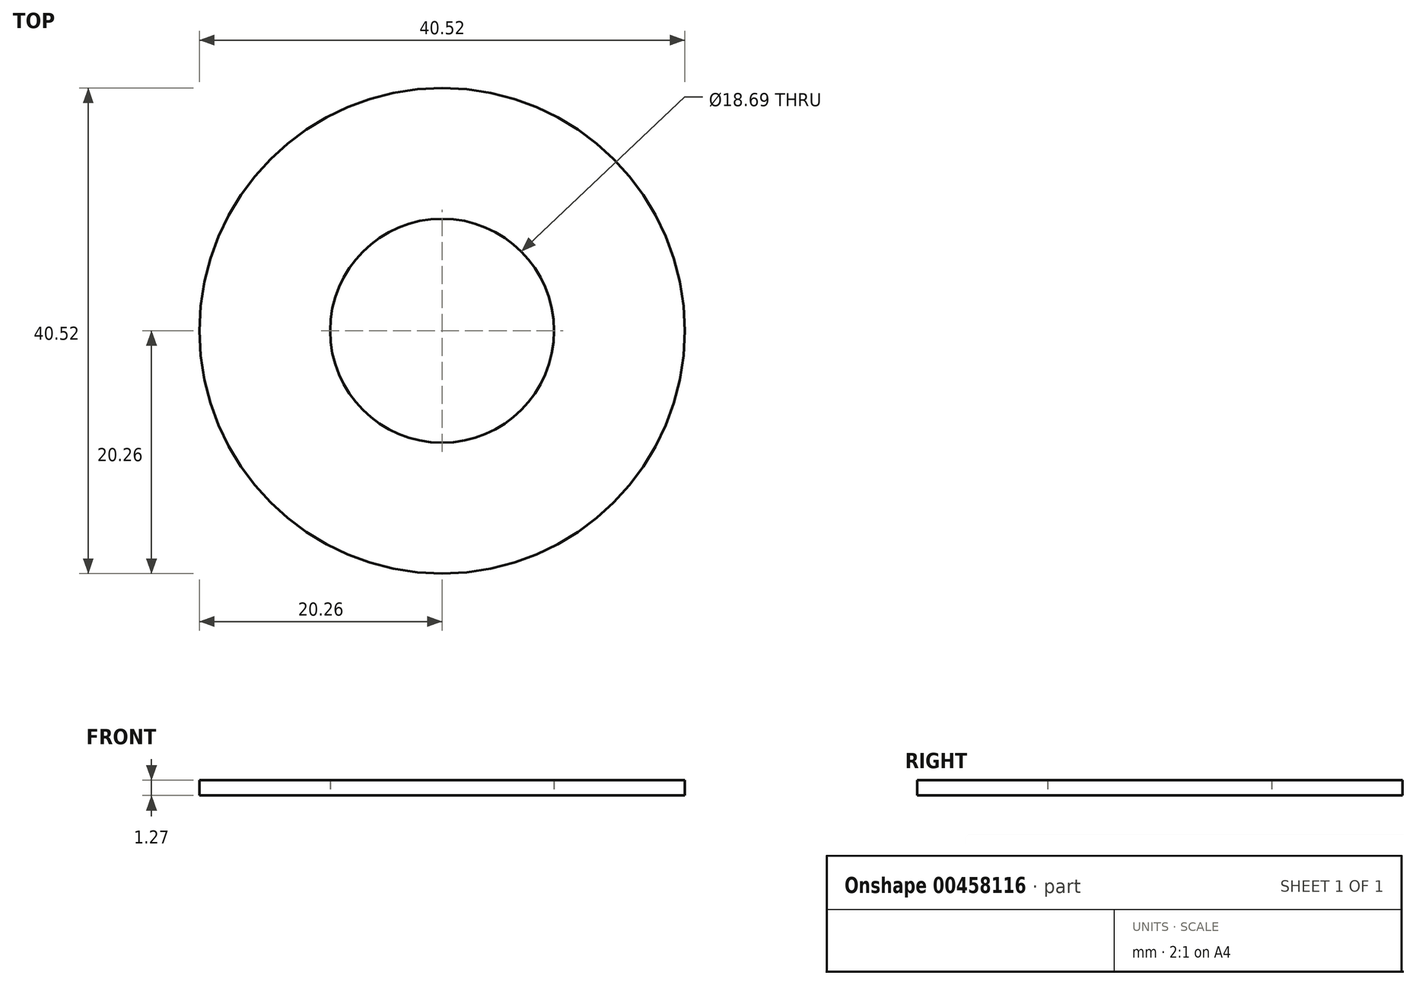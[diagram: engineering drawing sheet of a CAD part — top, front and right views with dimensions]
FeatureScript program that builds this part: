
annotation { "Feature Type Name" : "Feature", "Feature Type Description" : "" }
export const myFeature = defineFeature(function(context is Context, id is Id, definition is map)
    precondition{}
    {
        {
            var Q0;
            Q0=qCreatedBy(makeId("Top.planeOp"),FACE);
            var sketch = newSketch(context, id + "F0", { "sketchPlane" : qUnion([Q0])});
            skCircle(sketch, "E0", {"center": v(0, 0) * mm, "radius": 20.26 * mm});
            skCircle(sketch, "E1", {"center": v(0, 0) * mm, "radius": 9.35 * mm});
            skSolve(sketch);
        }
        {
            var Q0;
            Q0=makeQuery(id+"F0.imprint","IMPRINT",FACE,{"disambiguationData":[TD([[makeQuery(id+"F0.imprint","IMPRINT",EDGE,{"derivedFrom":sQuery(id+"F0.wireOp",EDGE,"E0")}),1.0]])]});
            extrude(context, id + "F1", {"entities" : qUnion([Q0]), "depth" : 1.27 * mm});
        }
    });
